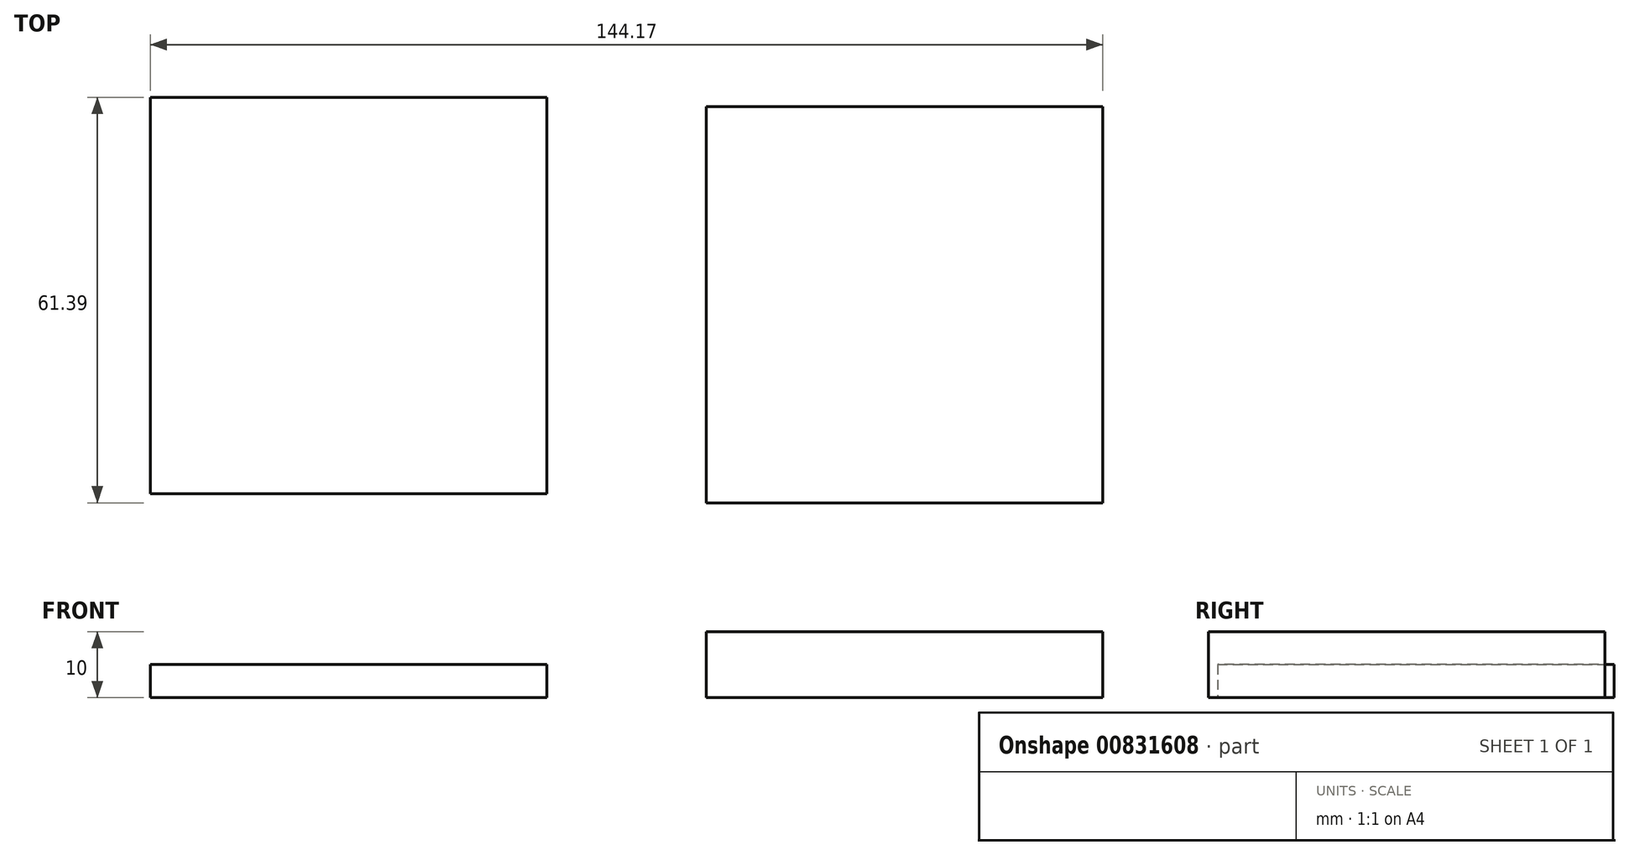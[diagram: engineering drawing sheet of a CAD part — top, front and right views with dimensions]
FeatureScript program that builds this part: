
annotation { "Feature Type Name" : "Feature", "Feature Type Description" : "" }
export const myFeature = defineFeature(function(context is Context, id is Id, definition is map)
    precondition{}
    {
        {
            var Q0;
            Q0=qCreatedBy(makeId("Top.planeOp"),FACE);
            var sketch = newSketch(context, id + "F0", { "sketchPlane" : qUnion([Q0])});
            skLineSegment(sketch, "E0", {"start": v(-77.64, 73.68) * mm, "end": v(-77.64, 13.68) * mm});
            skLineSegment(sketch, "E1", {"start": v(-77.64, 13.68) * mm, "end": v(-17.64, 13.68) * mm});
            skLineSegment(sketch, "E2", {"start": v(-17.64, 13.68) * mm, "end": v(-17.64, 73.68) * mm});
            skLineSegment(sketch, "E3", {"start": v(-17.64, 73.68) * mm, "end": v(-77.64, 73.68) * mm});
            skSolve(sketch);
        }
        {
            var Q0;
            Q0=makeQuery(id+"F0.imprint","IMPRINT",FACE,{"disambiguationData":[TD([[makeQuery(id+"F0.imprint","IMPRINT",EDGE,{"derivedFrom":sQuery(id+"F0.wireOp",EDGE,"E0")}),1.0]])]});
            extrude(context, id + "F1", {"entities" : qUnion([Q0]), "depth" : 5 * mm, "offsetDistance" : 25.4 * mm});
        }
        {
            var Q0;
            Q0=qCreatedBy(makeId("Top.planeOp"),FACE);
            var sketch = newSketch(context, id + "F2", { "sketchPlane" : qUnion([Q0])});
            skLineSegment(sketch, "E4", {"start": v(66.53, 12.3) * mm, "end": v(6.53, 12.3) * mm});
            skLineSegment(sketch, "E5", {"start": v(6.53, 72.3) * mm, "end": v(6.53, 12.3) * mm});
            skLineSegment(sketch, "E6", {"start": v(66.53, 12.3) * mm, "end": v(66.53, 72.3) * mm});
            skLineSegment(sketch, "E7", {"start": v(66.53, 72.3) * mm, "end": v(6.53, 72.3) * mm});
            skSolve(sketch);
        }
        {
            var Q0;
            Q0=makeQuery(id+"F2.imprint","IMPRINT",FACE,{"disambiguationData":[TD([[makeQuery(id+"F2.imprint","IMPRINT",EDGE,{"derivedFrom":sQuery(id+"F2.wireOp",EDGE,"E4")}),-1.0]])]});
            extrude(context, id + "F3", {"entities" : qUnion([Q0]), "depth" : 10 * mm, "offsetDistance" : 25 * mm});
        }
    });
